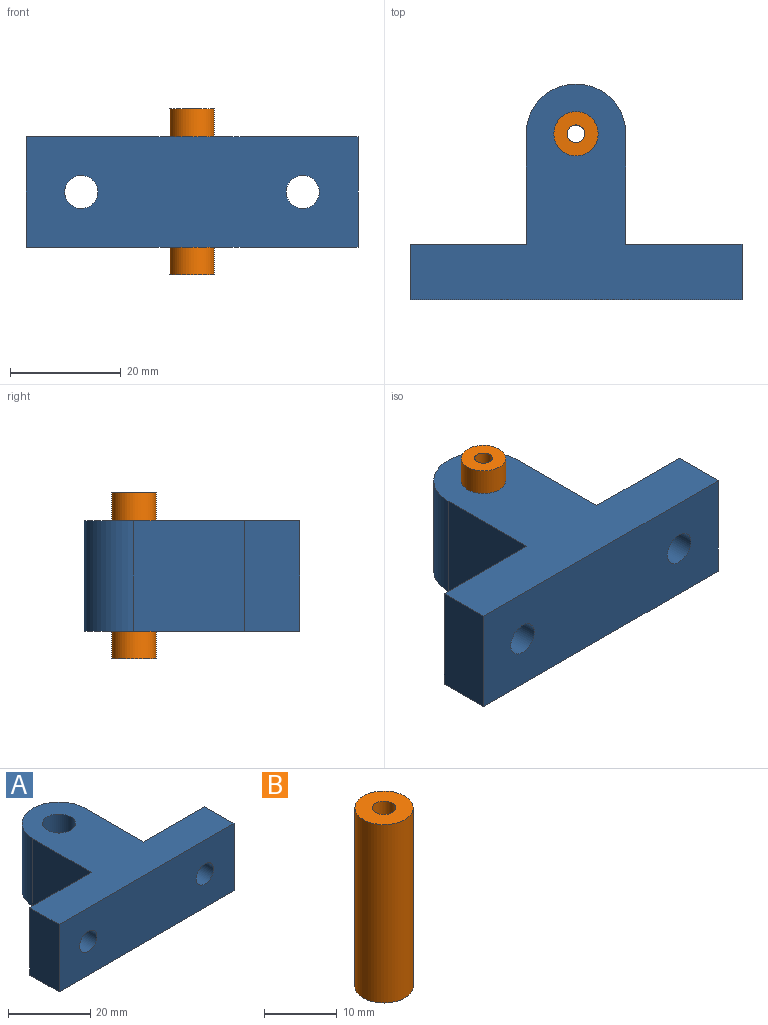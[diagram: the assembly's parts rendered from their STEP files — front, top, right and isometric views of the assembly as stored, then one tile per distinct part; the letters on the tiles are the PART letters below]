
ASSEMBLY  parts=2 mates=1
PART A: 17 faces, bbox 60x39x20 mm
  f0: cylinder r=3mm len=6mm, axis (0,1,0), area 94.2mm2, adj f8,f16
  f1: cylinder r=3mm len=6mm, axis (0,1,0), area 94.2mm2, adj f8,f14
  f2: plane 21x20mm, normal (0,1,0), area 333.4mm2, adj f3,f9,f11,f12,f15
  f3: plane 20x20mm, normal (1,0,0), area 400mm2, adj f2,f4,f11,f12
  f4: cylinder r=9mm len=20mm, axis (0,0,-1), area 565.5mm2, adj f3,f5,f11,f12
  f5: plane 20x20mm, normal (-1,0,0), area 400mm2, adj f4,f6,f11,f12
  f6: plane 21x20mm, normal (0,1,0), area 333.4mm2, adj f5,f7,f11,f12,f13
  f7: plane 20x10mm, normal (-1,0,0), area 200mm2, adj f6,f8,f11,f12
  f8: plane 60x20mm, normal (0,-1,0), area 1143.5mm2, adj f0,f1,f7,f9,f11,f12
  f9: plane 20x10mm, normal (1,0,0), area 200mm2, adj f2,f8,f11,f12
  f10: cylinder r=4mm len=20mm, axis (0,0,-1), area 502.7mm2, adj f11,f12
  f11: plane 60x39mm, normal (0,0,1), area 1037mm2, adj f2,f3,f4,f5,f6,f7,f8,f9
  f12: plane 60x39mm, normal (0,0,-1), area 1037mm2, adj f2,f3,f4,f5,f6,f7,f8,f9
  f13: cylinder r=5.25mm len=10.5mm, axis (0,1,0), area 164.9mm2, adj f6,f14
  f14: plane 10.5x10.5mm, normal (0,1,0), area 58.3mm2, adj f1,f13
  f15: cylinder r=5.25mm len=10.5mm, axis (0,1,0), area 164.9mm2, adj f2,f16
  f16: plane 10.5x10.5mm, normal (0,1,0), area 58.3mm2, adj f0,f15
PART B: 4 faces, bbox 8x8x30 mm
  f0: cylinder r=1.6mm len=30mm, axis (0,0,-1), area 301.6mm2, adj f2,f3
  f1: cylinder r=4mm len=30mm, axis (0,0,-1), area 754mm2, adj f2,f3
  f2: plane 8x8mm, normal (0,0,1), area 42.2mm2, adj f0,f1
  f3: plane 8x8mm, normal (0,0,-1), area 42.2mm2, adj f0,f1
PLACE A t=(-11.94,-15.4,3.99)mm
PLACE B t=(-11.94,9.6,-11.01)mm
MATE fastened B.f1 <-> A.f4  axis (0,0,-1) through (-11.94,9.6,3.99)mm
